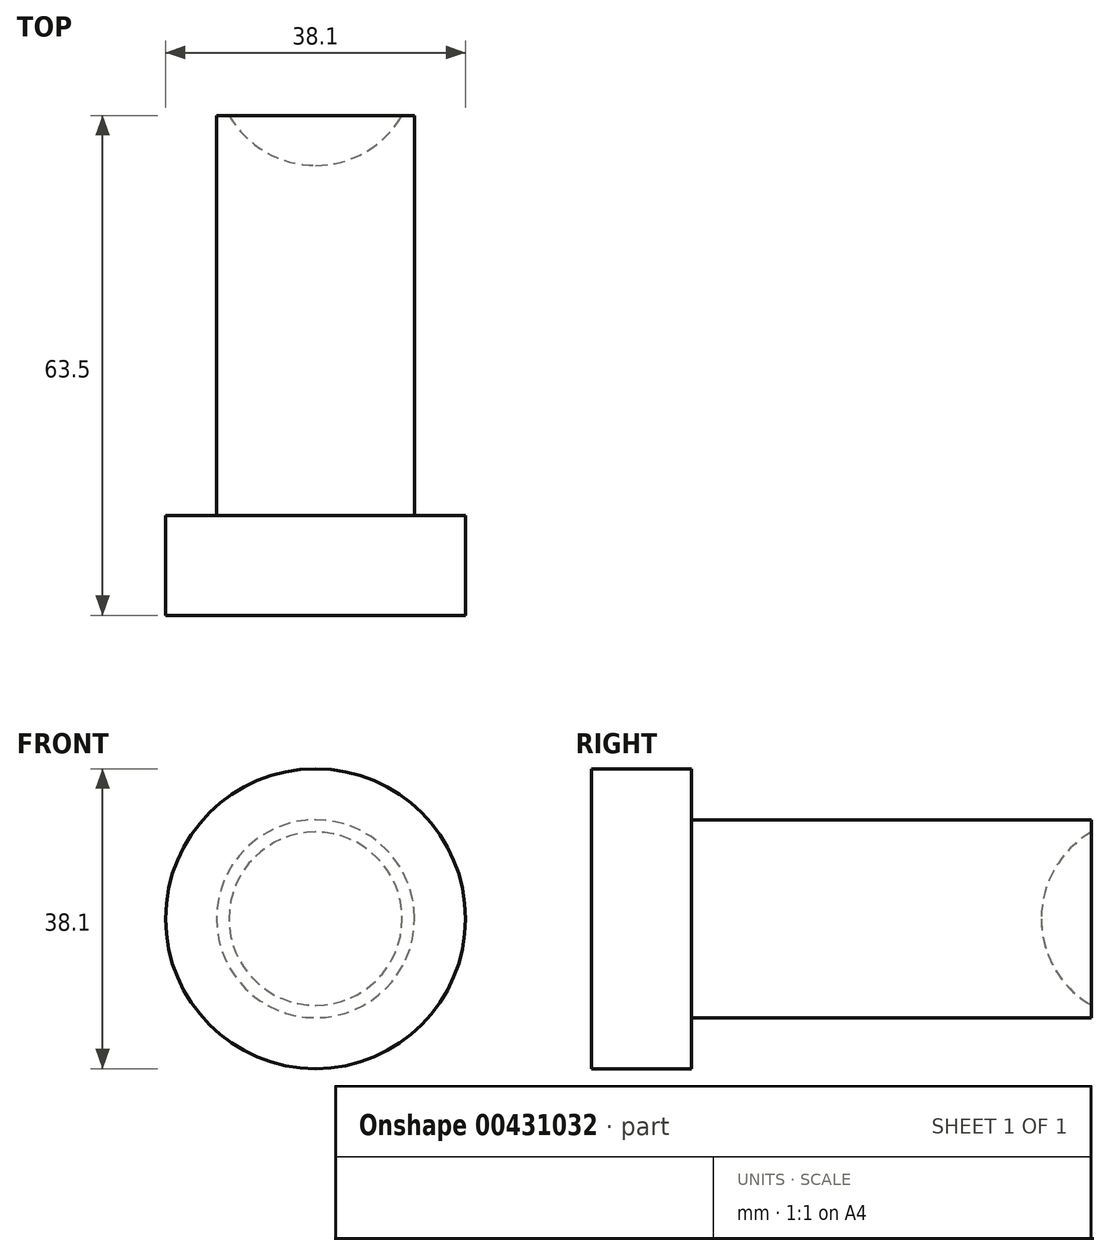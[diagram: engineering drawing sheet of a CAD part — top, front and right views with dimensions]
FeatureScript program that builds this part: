
annotation { "Feature Type Name" : "Feature", "Feature Type Description" : "" }
export const myFeature = defineFeature(function(context is Context, id is Id, definition is map)
    precondition{}
    {
        {
            var Q0;
            Q0=qCreatedBy(makeId("Front.planeOp"),FACE);
            var sketch = newSketch(context, id + "F0", { "sketchPlane" : qUnion([Q0])});
            skCircle(sketch, "E0", {"center": v(0, 0) * mm, "radius": 19.05 * mm});
            skSolve(sketch);
        }
        {
            var Q0;
            Q0=makeQuery(id+"F0.imprint","IMPRINT",FACE,{"disambiguationData":[TD([[makeQuery(id+"F0.imprint","IMPRINT",EDGE,{"derivedFrom":sQuery(id+"F0.wireOp",EDGE,"E0")}),1.0]])]});
            extrude(context, id + "F1", {"entities" : qUnion([Q0]), "depth" : 12.7 * mm});
        }
        {
            var Q0;
            Q0=makeQuery(id+"F1.opExtrude","CAP_FACE",FACE,{"disambiguationData":[OSD([sQuery(id+"F0.wireOp",EDGE,"E0")])],"isStart":true});
            var sketch = newSketch(context, id + "F2", { "sketchPlane" : qUnion([Q0])});
            skCircle(sketch, "E1", {"center": v(0, 0) * mm, "radius": 12.57 * mm});
            skSolve(sketch);
        }
        {
            var Q0;
            Q0=makeQuery(id+"F2.imprint","IMPRINT",FACE,{"disambiguationData":[TD([[makeQuery(id+"F2.imprint","IMPRINT",EDGE,{"derivedFrom":sQuery(id+"F2.wireOp",EDGE,"E1")}),1.0]])]});
            extrude(context, id + "F3", {"entities" : qUnion([Q0]), "operationType" : NewBodyOperationType.ADD, "depth" : 50.8 * mm});
        }
        {
            var Q0;
            Q0=qCreatedBy(makeId("Right.planeOp"),FACE);
            var sketch = newSketch(context, id + "F4", { "sketchPlane" : qUnion([Q0])});
            skLineSegment(sketch, "E2", {"start": v(57.15, 9.2) * mm, "end": v(57.15, -29.9) * mm});
            skLineSegment(sketch, "E3", {"start": v(0, 0) * mm, "end": v(57.15, 0) * mm});
            skCircle(sketch, "E4", {"center": v(57.15, 0) * mm, "radius": 12.7 * mm});
            skLineSegment(sketch, "E5", {"start": v(57.15, 0) * mm, "end": v(69.85, 0) * mm});
            skSolve(sketch);
        }
        {
            var Q0;
            {var subQ0=sQuery(id+"F4.wireOp",EDGE,"E5");Q0=makeQuery(id+"F4.imprint","IMPRINT",FACE,{"disambiguationData":[TD([[makeQuery(id+"F4.imprint","IMPRINT",EDGE,{"derivedFrom":subQ0}),1.0]])]});}
            var Q1;
            Q1=sQuery(id+"F4.wireOp",EDGE,"E5");
            revolve(context, id + "F5", {"operationType" : NewBodyOperationType.REMOVE, "entities" : qUnion([Q0]), "axis" : qUnion([Q1]), "revolveType" : RevolveType.FULL, "oppositeDirection" : true});
        }
    });
